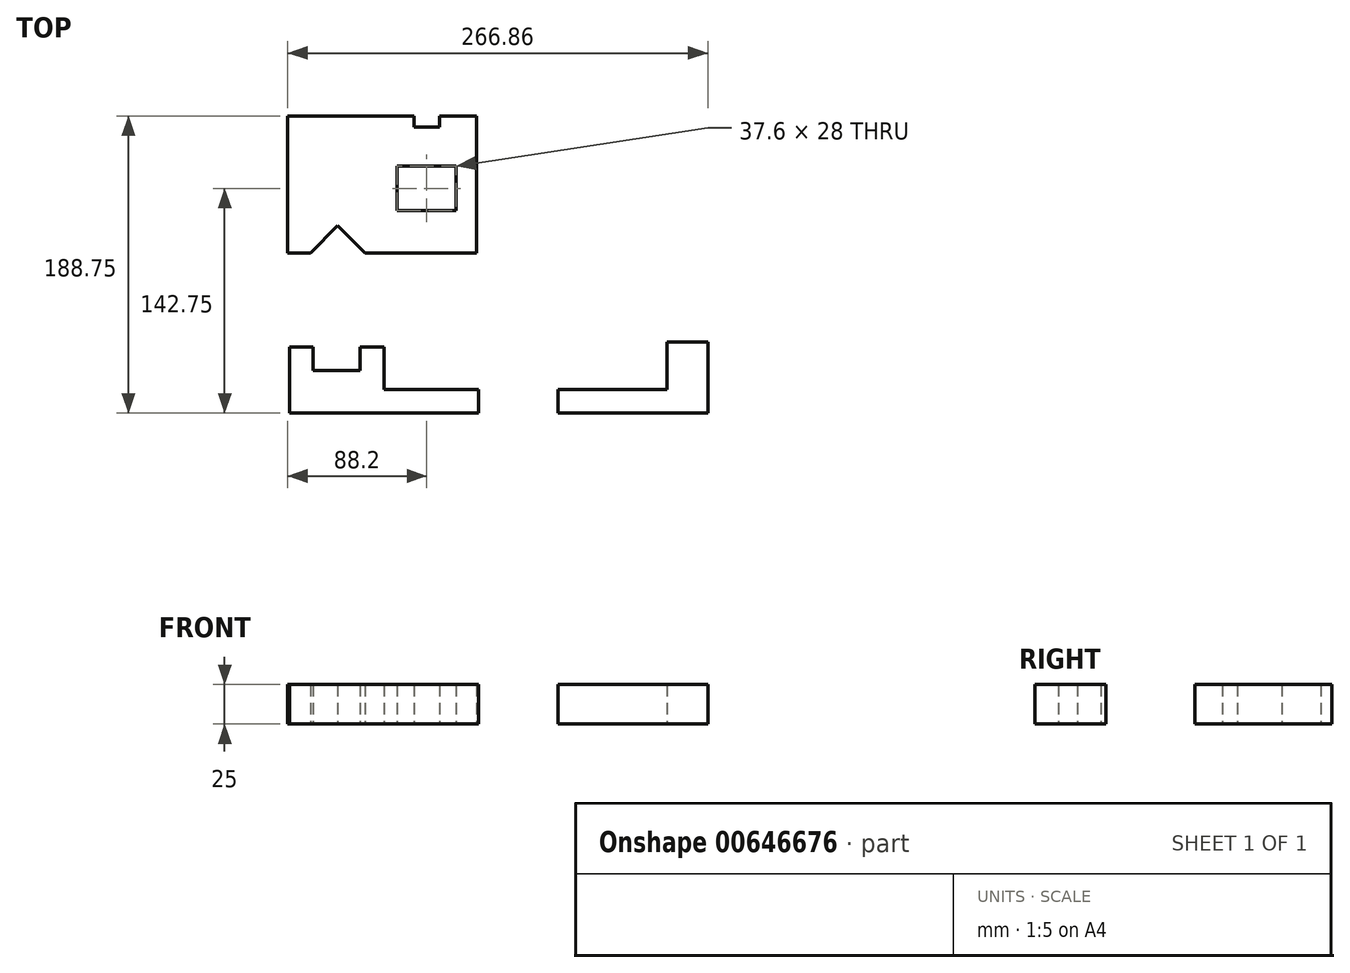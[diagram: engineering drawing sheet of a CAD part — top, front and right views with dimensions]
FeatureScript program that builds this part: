
annotation { "Feature Type Name" : "Feature", "Feature Type Description" : "" }
export const myFeature = defineFeature(function(context is Context, id is Id, definition is map)
    precondition{}
    {
        {
            var Q0;
            Q0=qCreatedBy(makeId("Top.planeOp"),FACE);
            var sketch = newSketch(context, id + "F0", { "sketchPlane" : qUnion([Q0])});
            skLineSegment(sketch, "E0", {"start": v(-60, 0) * mm, "end": v(-60, 61) * mm});
            skLineSegment(sketch, "E1", {"start": v(-60, 61) * mm, "end": v(-60, 87) * mm});
            skLineSegment(sketch, "E2", {"start": v(-60, 87) * mm, "end": v(-45, 87) * mm});
            skLineSegment(sketch, "E3", {"start": v(-45, 87) * mm, "end": v(-15, 87) * mm});
            skLineSegment(sketch, "E4", {"start": v(-15, 87) * mm, "end": v(0, 87) * mm});
            skLineSegment(sketch, "E5", {"start": v(0, 87) * mm, "end": v(20.35, 87) * mm});
            skLineSegment(sketch, "E6", {"start": v(20.35, 87) * mm, "end": v(20.35, 80) * mm});
            skLineSegment(sketch, "E7", {"start": v(20.35, 80) * mm, "end": v(36.35, 80) * mm});
            skLineSegment(sketch, "E8", {"start": v(36.35, 80) * mm, "end": v(36.35, 87) * mm});
            skLineSegment(sketch, "E9", {"start": v(36.35, 87) * mm, "end": v(60, 87) * mm});
            skLineSegment(sketch, "E10", {"start": v(60, 87) * mm, "end": v(60, 0) * mm});
            skLineSegment(sketch, "E11", {"start": v(60, 0) * mm, "end": v(-11, 0) * mm});
            skLineSegment(sketch, "E12", {"start": v(-45.5, 0) * mm, "end": v(-60, 0) * mm});
            skLineSegment(sketch, "E13", {"start": v(-60, 61) * mm, "end": v(-45, 61) * mm});
            skLineSegment(sketch, "E14", {"start": v(-45, 61) * mm, "end": v(-45, 87) * mm});
            skLineSegment(sketch, "E15", {"start": v(-45, 61) * mm, "end": v(-15, 61) * mm});
            skLineSegment(sketch, "E16", {"start": v(-15, 61) * mm, "end": v(-15, 87) * mm});
            skLineSegment(sketch, "E17", {"start": v(-15, 61) * mm, "end": v(0, 61) * mm});
            skLineSegment(sketch, "E18", {"start": v(0, 61) * mm, "end": v(0, 87) * mm});
            skLineSegment(sketch, "E19", {"start": v(47, 27) * mm, "end": v(9.4, 27) * mm});
            skLineSegment(sketch, "E20", {"start": v(9.4, 27) * mm, "end": v(9.4, 55) * mm});
            skLineSegment(sketch, "E21", {"start": v(9.4, 55) * mm, "end": v(47, 55) * mm});
            skLineSegment(sketch, "E22", {"start": v(47, 27) * mm, "end": v(47, 55) * mm});
            skLineSegment(sketch, "E23", {"start": v(-28.25, 17.25) * mm, "end": v(-11, 0) * mm});
            skLineSegment(sketch, "E24", {"start": v(-28.25, 17.25) * mm, "end": v(-45.5, 0) * mm});
            skLineSegment(sketch, "E25", {"start": v(-58.91, -59.75) * mm, "end": v(-58.91, -86.75) * mm});
            skLineSegment(sketch, "E26", {"start": v(-58.91, -86.75) * mm, "end": v(-58.91, -101.75) * mm});
            skLineSegment(sketch, "E27", {"start": v(-58.91, -101.75) * mm, "end": v(-44.41, -101.75) * mm});
            skLineSegment(sketch, "E28", {"start": v(-27.16, -101.75) * mm, "end": v(-9.91, -101.75) * mm});
            skLineSegment(sketch, "E29", {"start": v(10.49, -101.75) * mm, "end": v(25.09, -101.75) * mm});
            skLineSegment(sketch, "E30", {"start": v(25.09, -101.75) * mm, "end": v(41.09, -101.75) * mm});
            skLineSegment(sketch, "E31", {"start": v(-44.41, -101.75) * mm, "end": v(-44.41, -86.75) * mm});
            skLineSegment(sketch, "E32", {"start": v(-9.91, -101.75) * mm, "end": v(-9.91, -86.75) * mm});
            skLineSegment(sketch, "E33", {"start": v(-27.16, -101.75) * mm, "end": v(-27.16, -86.75) * mm});
            skLineSegment(sketch, "E34", {"start": v(10.49, -101.75) * mm, "end": v(10.49, -86.75) * mm, "construction": true});
            skLineSegment(sketch, "E35", {"start": v(25.09, -101.75) * mm, "end": v(25.09, -86.75) * mm, "construction": true});
            skLineSegment(sketch, "E36", {"start": v(41.09, -101.75) * mm, "end": v(41.09, -86.75) * mm, "construction": true});
            skLineSegment(sketch, "E37", {"start": v(-58.91, -86.75) * mm, "end": v(-44.41, -86.75) * mm});
            skLineSegment(sketch, "E38", {"start": v(10.49, -86.75) * mm, "end": v(25.09, -86.75) * mm});
            skLineSegment(sketch, "E39", {"start": v(25.09, -86.75) * mm, "end": v(41.09, -86.75) * mm});
            skLineSegment(sketch, "E40", {"start": v(41.09, -101.75) * mm, "end": v(48.09, -101.75) * mm});
            skLineSegment(sketch, "E41", {"start": v(48.09, -101.75) * mm, "end": v(61.09, -101.75) * mm});
            skLineSegment(sketch, "E42", {"start": v(61.09, -101.75) * mm, "end": v(61.09, -86.75) * mm});
            skLineSegment(sketch, "E43", {"start": v(48.09, -101.75) * mm, "end": v(48.09, -86.75) * mm, "construction": true});
            skLineSegment(sketch, "E44", {"start": v(41.09, -86.75) * mm, "end": v(48.09, -86.75) * mm});
            skLineSegment(sketch, "E45", {"start": v(48.09, -86.75) * mm, "end": v(61.09, -86.75) * mm});
            skLineSegment(sketch, "E46", {"start": v(-58.91, -59.75) * mm, "end": v(-43.91, -59.75) * mm});
            skLineSegment(sketch, "E47", {"start": v(-43.91, -59.75) * mm, "end": v(-43.91, -74.75) * mm});
            skLineSegment(sketch, "E48", {"start": v(-43.91, -74.75) * mm, "end": v(-13.91, -74.75) * mm});
            skLineSegment(sketch, "E49", {"start": v(-13.91, -74.75) * mm, "end": v(-13.91, -59.75) * mm});
            skLineSegment(sketch, "E50", {"start": v(-13.91, -59.75) * mm, "end": v(1.09, -59.75) * mm});
            skLineSegment(sketch, "E51", {"start": v(1.09, -59.75) * mm, "end": v(1.09, -86.75) * mm});
            skLineSegment(sketch, "E52", {"start": v(-9.91, -101.75) * mm, "end": v(10.49, -101.75) * mm});
            skLineSegment(sketch, "E53", {"start": v(-44.41, -101.75) * mm, "end": v(-27.16, -101.75) * mm});
            skLineSegment(sketch, "E54", {"start": v(10.49, -86.75) * mm, "end": v(-9.91, -86.75) * mm});
            skLineSegment(sketch, "E55", {"start": v(-9.91, -86.75) * mm, "end": v(1.09, -86.75) * mm});
            skLineSegment(sketch, "E56", {"start": v(1.09, -86.75) * mm, "end": v(-27.16, -86.75) * mm});
            skLineSegment(sketch, "E57", {"start": v(-27.16, -86.75) * mm, "end": v(-44.41, -86.75) * mm});
            skLineSegment(sketch, "E58", {"start": v(111.6, -101.75) * mm, "end": v(133.5, -101.75) * mm});
            skLineSegment(sketch, "E59", {"start": v(133.5, -101.75) * mm, "end": v(142.5, -101.75) * mm});
            skLineSegment(sketch, "E60", {"start": v(142.5, -101.75) * mm, "end": v(167.73, -101.75) * mm});
            skLineSegment(sketch, "E61", {"start": v(167.73, -101.75) * mm, "end": v(196.56, -101.75) * mm});
            skLineSegment(sketch, "E62", {"start": v(196.56, -101.75) * mm, "end": v(206.86, -101.75) * mm});
            skLineSegment(sketch, "E63", {"start": v(206.86, -101.75) * mm, "end": v(206.86, -86.75) * mm});
            skLineSegment(sketch, "E64", {"start": v(206.86, -86.75) * mm, "end": v(206.86, -71.75) * mm});
            skLineSegment(sketch, "E65", {"start": v(206.86, -71.75) * mm, "end": v(206.86, -56.75) * mm});
            skLineSegment(sketch, "E66", {"start": v(206.86, -56.75) * mm, "end": v(180.86, -56.75) * mm});
            skLineSegment(sketch, "E67", {"start": v(111.6, -101.75) * mm, "end": v(111.6, -86.75) * mm});
            skLineSegment(sketch, "E68", {"start": v(133.5, -101.75) * mm, "end": v(133.5, -86.75) * mm, "construction": true});
            skLineSegment(sketch, "E69", {"start": v(142.5, -101.75) * mm, "end": v(142.5, -86.75) * mm, "construction": true});
            skLineSegment(sketch, "E70", {"start": v(167.73, -101.75) * mm, "end": v(167.73, -86.75) * mm, "construction": true});
            skLineSegment(sketch, "E71", {"start": v(196.56, -101.75) * mm, "end": v(196.56, -86.75) * mm, "construction": true});
            skLineSegment(sketch, "E72", {"start": v(111.6, -86.75) * mm, "end": v(133.5, -86.75) * mm});
            skLineSegment(sketch, "E73", {"start": v(133.5, -86.75) * mm, "end": v(142.5, -86.75) * mm});
            skLineSegment(sketch, "E74", {"start": v(142.5, -86.75) * mm, "end": v(167.73, -86.75) * mm});
            skLineSegment(sketch, "E75", {"start": v(167.73, -86.75) * mm, "end": v(196.56, -86.75) * mm});
            skLineSegment(sketch, "E76", {"start": v(196.56, -86.75) * mm, "end": v(206.86, -86.75) * mm});
            skLineSegment(sketch, "E77", {"start": v(206.86, -71.75) * mm, "end": v(180.86, -71.75) * mm, "construction": true});
            skLineSegment(sketch, "E78", {"start": v(180.86, -56.75) * mm, "end": v(180.86, -71.75) * mm});
            skLineSegment(sketch, "E79", {"start": v(180.86, -71.75) * mm, "end": v(180.86, -86.75) * mm});
            skSolve(sketch);
        }
        {
            var Q0;
            Q0 = qSketchRegion(id + "F0", true);
            extrude(context, id + "F1", {"entities" : qUnion([Q0]), "depth" : 25 * mm, "offsetDistance" : 25 * mm});
        }
    });
